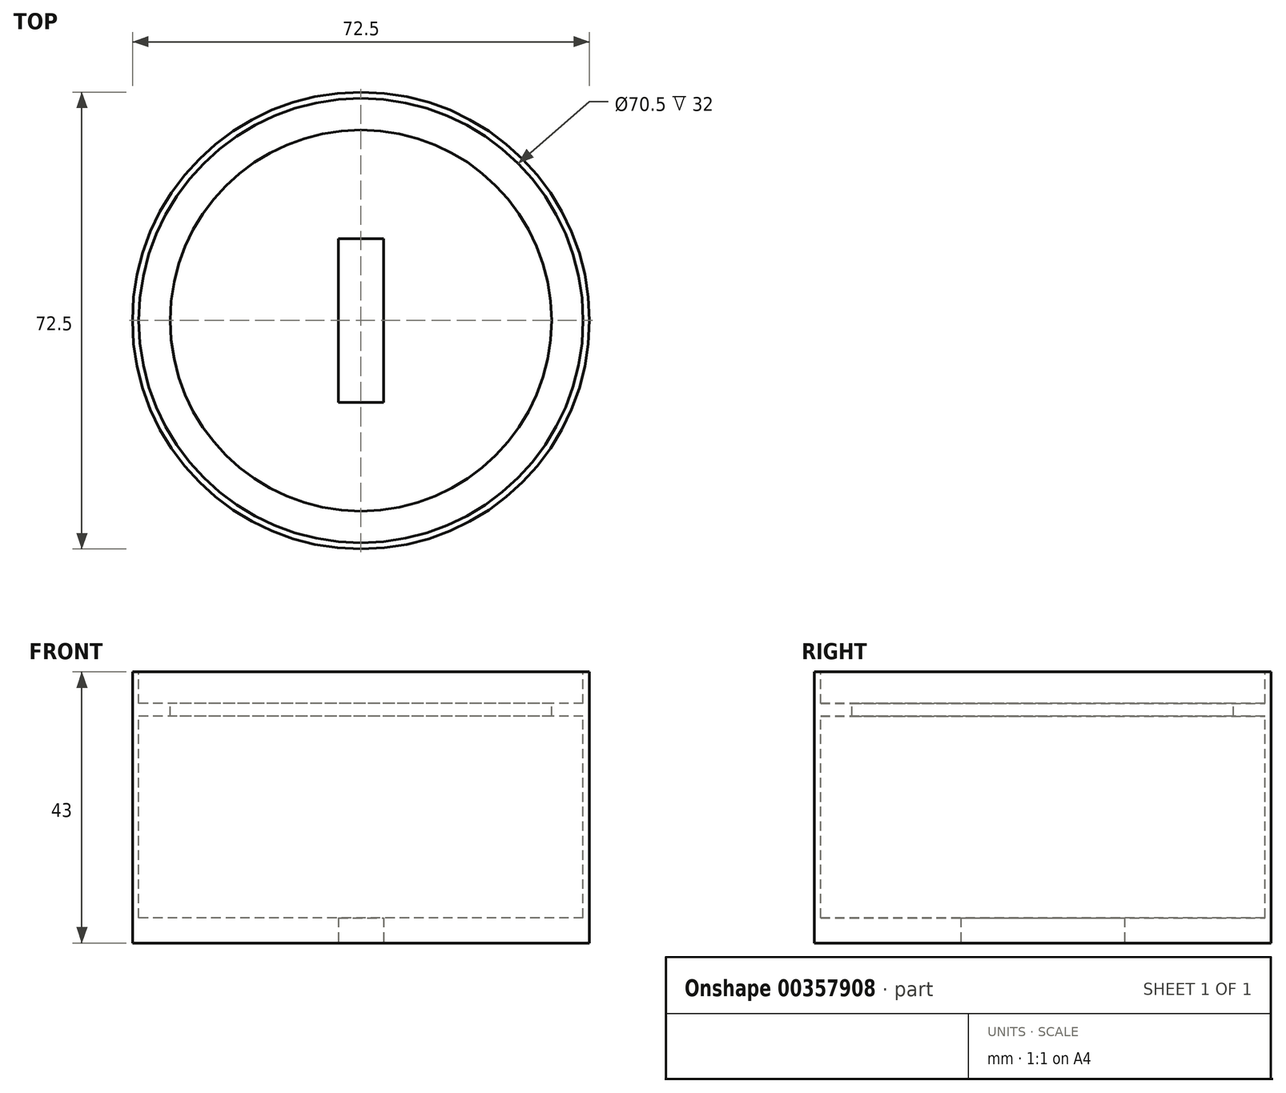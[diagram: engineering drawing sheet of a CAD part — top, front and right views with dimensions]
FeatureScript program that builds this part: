
annotation { "Feature Type Name" : "Feature", "Feature Type Description" : "" }
export const myFeature = defineFeature(function(context is Context, id is Id, definition is map)
    precondition{}
    {
        {
            var Q0;
            Q0=qCreatedBy(makeId("Top.planeOp"),FACE);
            var sketch = newSketch(context, id + "F0", { "sketchPlane" : qUnion([Q0])});
            skCircle(sketch, "E0", {"center": v(0, 0) * mm, "radius": 36.25 * mm});
            skSolve(sketch);
        }
        {
            var Q0;
            Q0=makeQuery(id+"F0.imprint","IMPRINT",FACE,{"disambiguationData":[TD([[makeQuery(id+"F0.imprint","IMPRINT",EDGE,{"derivedFrom":sQuery(id+"F0.wireOp",EDGE,"E0")}),1.0]])]});
            extrude(context, id + "F1", {"entities" : qUnion([Q0]), "depth" : 43 * mm});
        }
        {
            var Q0;
            Q0=makeQuery(id+"F1.opExtrude","CAP_FACE",FACE,{"disambiguationData":[OSD([sQuery(id+"F0.wireOp",EDGE,"E0")])],"isStart":false});
            var sketch = newSketch(context, id + "F2", { "sketchPlane" : qUnion([Q0])});
            skCircle(sketch, "E1", {"center": v(0, 0) * mm, "radius": 35.25 * mm});
            skSolve(sketch);
        }
        {
            var Q0;
            Q0 = qSketchRegion(id + "F2", true);
            extrude(context, id + "F3", {"entities" : qUnion([Q0]), "operationType" : NewBodyOperationType.REMOVE, "oppositeDirection" : true, "depth" : 39 * mm});
        }
        {
            var Q0;
            Q0=qCreatedBy(makeId("Top.planeOp"),FACE);
            cPlane(context, id + "F4", {"entities" : qUnion([Q0]), "cplaneType" : CPlaneType.OFFSET, "offset" : 38 * mm, "width" : 150 * mm, "height" : 150 * mm});
        }
        {
            var Q0;
            Q0=qCreatedBy(id+"F4.planeOp",FACE);
            var sketch = newSketch(context, id + "F5", { "sketchPlane" : qUnion([Q0])});
            skCircle(sketch, "E2", {"center": v(0, 0) * mm, "radius": 36.25 * mm});
            skCircle(sketch, "E3", {"center": v(0, 0) * mm, "radius": 30.25 * mm});
            skSolve(sketch);
        }
        {
            var Q0;
            Q0 = qSketchRegion(id + "F5", true);
            extrude(context, id + "F6", {"entities" : qUnion([Q0]), "operationType" : NewBodyOperationType.ADD, "oppositeDirection" : true, "depth" : 2 * mm});
        }
        {
            var Q0;
            Q0=qCreatedBy(makeId("Top.planeOp"),FACE);
            var sketch = newSketch(context, id + "F7", { "sketchPlane" : qUnion([Q0])});
            skLineSegment(sketch, "E4.bottom", {"start": v(3.58, 13) * mm, "end": v(-3.59, 13) * mm});
            skLineSegment(sketch, "E4.top", {"start": v(3.58, -13) * mm, "end": v(-3.58, -13) * mm});
            skLineSegment(sketch, "E4.left", {"start": v(3.58, 13) * mm, "end": v(3.58, -13) * mm});
            skLineSegment(sketch, "E4.right", {"start": v(-3.59, 13) * mm, "end": v(-3.58, -13) * mm});
            skPoint(sketch, "E4.middle", {"position": v(0, 0) * mm});
            skSolve(sketch);
        }
        {
            var Q0;
            Q0=makeQuery(id+"F7.imprint","IMPRINT",FACE,{"disambiguationData":[TD([[makeQuery(id+"F7.imprint","IMPRINT",EDGE,{"derivedFrom":sQuery(id+"F7.wireOp",EDGE,"E4.bottom")}),1.0]])]});
            extrude(context, id + "F8", {"entities" : qUnion([Q0]), "operationType" : NewBodyOperationType.REMOVE, "endBound" : BoundingType.THROUGH_ALL, "depth" : 25 * mm});
        }
    });
